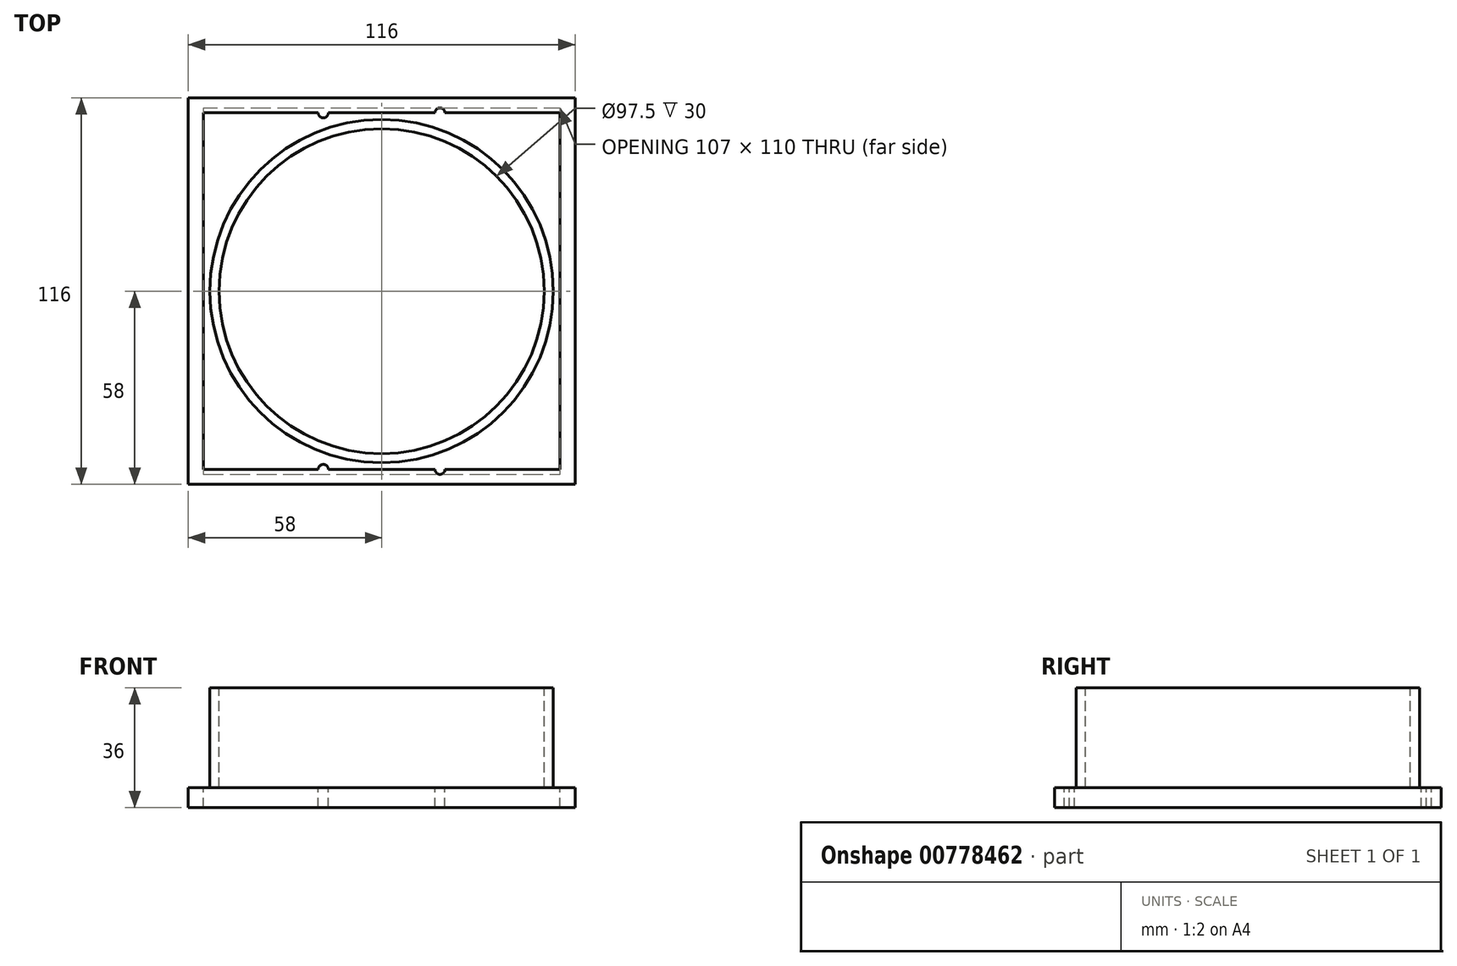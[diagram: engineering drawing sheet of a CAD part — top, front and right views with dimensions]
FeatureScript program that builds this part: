
annotation { "Feature Type Name" : "Feature", "Feature Type Description" : "" }
export const myFeature = defineFeature(function(context is Context, id is Id, definition is map)
    precondition{}
    {
        {
            var Q0;
            Q0=qCreatedBy(makeId("Top.planeOp"),FACE);
            var sketch = newSketch(context, id + "F0", { "sketchPlane" : qUnion([Q0])});
            skLineSegment(sketch, "E0.bottom", {"start": v(53.5, -53.5) * mm, "end": v(-53.5, -53.5) * mm});
            skLineSegment(sketch, "E0.top", {"start": v(53.5, 53.5) * mm, "end": v(-53.5, 53.5) * mm});
            skLineSegment(sketch, "E0.left", {"start": v(53.5, -53.5) * mm, "end": v(53.5, 53.5) * mm});
            skLineSegment(sketch, "E0.right", {"start": v(-53.5, -53.5) * mm, "end": v(-53.5, 53.5) * mm});
            skPoint(sketch, "E0.middle", {"position": v(0, 0) * mm});
            skCircle(sketch, "E1", {"center": v(-17.5, 53.5) * mm, "radius": 1.5 * mm});
            skCircle(sketch, "E2", {"center": v(17.5, 53.5) * mm, "radius": 1.5 * mm});
            skCircle(sketch, "E3", {"center": v(-17.5, -53.5) * mm, "radius": 1.5 * mm});
            skCircle(sketch, "E4", {"center": v(17.5, -53.5) * mm, "radius": 1.5 * mm});
            skSolve(sketch);
        }
        {
            var Q0;
            Q0=qCreatedBy(makeId("Top.planeOp"),FACE);
            var sketch = newSketch(context, id + "F1", { "sketchPlane" : qUnion([Q0])});
            skLineSegment(sketch, "E5.bottom", {"start": v(58, -58) * mm, "end": v(-58, -58) * mm});
            skLineSegment(sketch, "E5.top", {"start": v(58, 58) * mm, "end": v(-58, 58) * mm});
            skLineSegment(sketch, "E5.left", {"start": v(58, -58) * mm, "end": v(58, 58) * mm});
            skLineSegment(sketch, "E5.right", {"start": v(-58, -58) * mm, "end": v(-58, 58) * mm});
            skPoint(sketch, "E5.middle", {"position": v(0, 0) * mm});
            skCircle(sketch, "E6", {"center": v(0, 0) * mm, "radius": 48.75 * mm});
            skCircle(sketch, "E7", {"center": v(0, 0) * mm, "radius": 51.5 * mm});
            skSolve(sketch);
        }
        {
            var Q0;
            Q0=makeQuery(id+"F1.imprint","IMPRINT",FACE,{"disambiguationData":[TD([[makeQuery(id+"F1.imprint","IMPRINT",EDGE,{"derivedFrom":sQuery(id+"F1.wireOp",EDGE,"E5.bottom")}),-1.0]])]});
            var Q1;
            Q1=makeQuery(id+"F1.imprint","IMPRINT",FACE,{"disambiguationData":[TD([[makeQuery(id+"F1.imprint","IMPRINT",EDGE,{"derivedFrom":sQuery(id+"F1.wireOp",EDGE,"E6")}),-1.0]])]});
            extrude(context, id + "F2", {"entities" : qUnion([Q0, Q1]), "depth" : -6 * mm, "offsetDistance" : 25 * mm});
        }
        {
            var Q0;
            Q0=makeQuery(id+"F1.imprint","IMPRINT",FACE,{"disambiguationData":[TD([[makeQuery(id+"F1.imprint","IMPRINT",EDGE,{"derivedFrom":sQuery(id+"F1.wireOp",EDGE,"E6")}),-1.0]])]});
            extrude(context, id + "F3", {"entities" : qUnion([Q0]), "operationType" : NewBodyOperationType.ADD, "depth" : 30 * mm, "offsetDistance" : 25 * mm});
        }
        {
            var Q0;
            {var subQ0=sQuery(id+"F0.wireOp",EDGE,"E2");var subQ1=sQuery(id+"F0.wireOp",EDGE,"E0.top");var subQ2=makeQuery(id+"F0.imprint","INTERSECT",VERTEX,{"disambiguationData":[OD(0.0)],"derivedFrom":[subQ1,subQ0]});Q0=makeQuery(id+"F0.imprint","IMPRINT",FACE,{"disambiguationData":[TD([[makeQuery(id+"F0.imprint","IMPRINT",EDGE,{"disambiguationData":[TD([[subQ2,-1.0]])],"derivedFrom":subQ1}),-1.0]])]});}
            var Q1;
            {var subQ0=sQuery(id+"F0.wireOp",EDGE,"E2");var subQ1=sQuery(id+"F0.wireOp",EDGE,"E0.top");var subQ2=makeQuery(id+"F0.imprint","INTERSECT",VERTEX,{"disambiguationData":[OD(0.0)],"derivedFrom":[subQ1,subQ0]});Q1=makeQuery(id+"F0.imprint","IMPRINT",FACE,{"disambiguationData":[TD([[makeQuery(id+"F0.imprint","IMPRINT",EDGE,{"disambiguationData":[TD([[subQ2,-1.0]])],"derivedFrom":subQ1}),1.0]])]});}
            extrude(context, id + "F4", {"entities" : qUnion([Q0, Q1]), "operationType" : NewBodyOperationType.REMOVE, "oppositeDirection" : true, "depth" : 6 * mm, "offsetDistance" : 25 * mm});
        }
        {
            var Q0;
            {var subQ0=sQuery(id+"F0.wireOp",EDGE,"E4");var subQ1=sQuery(id+"F0.wireOp",EDGE,"E0.bottom");var subQ2=makeQuery(id+"F0.imprint","INTERSECT",VERTEX,{"disambiguationData":[OD(0.0)],"derivedFrom":[subQ1,subQ0]});Q0=makeQuery(id+"F0.imprint","IMPRINT",FACE,{"disambiguationData":[TD([[makeQuery(id+"F0.imprint","IMPRINT",EDGE,{"disambiguationData":[TD([[subQ2,-1.0]])],"derivedFrom":subQ1}),-1.0]])]});}
            var Q1;
            {var subQ0=sQuery(id+"F0.wireOp",EDGE,"E4");var subQ1=sQuery(id+"F0.wireOp",EDGE,"E0.bottom");var subQ2=makeQuery(id+"F0.imprint","INTERSECT",VERTEX,{"disambiguationData":[OD(0.0)],"derivedFrom":[subQ1,subQ0]});Q1=makeQuery(id+"F0.imprint","IMPRINT",FACE,{"disambiguationData":[TD([[makeQuery(id+"F0.imprint","IMPRINT",EDGE,{"disambiguationData":[TD([[subQ2,-1.0]])],"derivedFrom":subQ1}),1.0]])]});}
            var Q2;
            {var subQ0=sQuery(id+"F0.wireOp",EDGE,"E3");var subQ1=sQuery(id+"F0.wireOp",EDGE,"E0.bottom");var subQ2=makeQuery(id+"F0.imprint","INTERSECT",VERTEX,{"disambiguationData":[OD(0.0)],"derivedFrom":[subQ1,subQ0]});Q2=makeQuery(id+"F0.imprint","IMPRINT",FACE,{"disambiguationData":[TD([[makeQuery(id+"F0.imprint","IMPRINT",EDGE,{"disambiguationData":[TD([[subQ2,-1.0]])],"derivedFrom":subQ1}),-1.0]])]});}
            var Q3;
            {var subQ0=sQuery(id+"F0.wireOp",EDGE,"E3");var subQ1=sQuery(id+"F0.wireOp",EDGE,"E0.bottom");var subQ2=makeQuery(id+"F0.imprint","INTERSECT",VERTEX,{"disambiguationData":[OD(0.0)],"derivedFrom":[subQ1,subQ0]});Q3=makeQuery(id+"F0.imprint","IMPRINT",FACE,{"disambiguationData":[TD([[makeQuery(id+"F0.imprint","IMPRINT",EDGE,{"disambiguationData":[TD([[subQ2,-1.0]])],"derivedFrom":subQ1}),1.0]])]});}
            var Q4;
            {var subQ0=sQuery(id+"F0.wireOp",EDGE,"E1");var subQ1=sQuery(id+"F0.wireOp",EDGE,"E0.top");var subQ2=makeQuery(id+"F0.imprint","INTERSECT",VERTEX,{"disambiguationData":[OD(0.0)],"derivedFrom":[subQ1,subQ0]});Q4=makeQuery(id+"F0.imprint","IMPRINT",FACE,{"disambiguationData":[TD([[makeQuery(id+"F0.imprint","IMPRINT",EDGE,{"disambiguationData":[TD([[subQ2,-1.0]])],"derivedFrom":subQ1}),1.0]])]});}
            var Q5;
            {var subQ0=sQuery(id+"F0.wireOp",EDGE,"E1");var subQ1=sQuery(id+"F0.wireOp",EDGE,"E0.top");var subQ2=makeQuery(id+"F0.imprint","INTERSECT",VERTEX,{"disambiguationData":[OD(0.0)],"derivedFrom":[subQ1,subQ0]});Q5=makeQuery(id+"F0.imprint","IMPRINT",FACE,{"disambiguationData":[TD([[makeQuery(id+"F0.imprint","IMPRINT",EDGE,{"disambiguationData":[TD([[subQ2,-1.0]])],"derivedFrom":subQ1}),-1.0]])]});}
            extrude(context, id + "F5", {"entities" : qUnion([Q0, Q1, Q2, Q3, Q4, Q5]), "operationType" : NewBodyOperationType.REMOVE, "oppositeDirection" : true, "depth" : 6 * mm, "offsetDistance" : 25 * mm});
        }
        {
            var Q0;
            Q0=makeQuery(id+"F2.opExtrude","SWEPT_BODY",BODY,{"disambiguationData":[OSD([sQuery(id+"F1.wireOp",EDGE,"E5.bottom"),sQuery(id+"F1.wireOp",EDGE,"E5.top"),sQuery(id+"F1.wireOp",EDGE,"E5.left"),sQuery(id+"F1.wireOp",EDGE,"E5.right"),sQuery(id+"F1.wireOp",EDGE,"E6")])]});
            var Q1;
            Q1=qCreatedBy(makeId("Top.planeOp"),FACE);
            transform(context, id + "F6", {"entities" : qUnion([Q0]), "transformType" : TransformType.TRANSLATION_DISTANCE, "transformDirection" : qUnion([Q1]), "distance" : 6 * mm, "makeCopy" : false});
        }
    });
